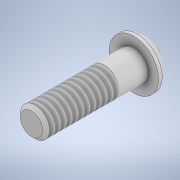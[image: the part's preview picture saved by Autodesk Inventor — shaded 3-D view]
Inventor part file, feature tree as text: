
AUTODESK INVENTOR PART (.ipt)
format: ipt  version: 2020 (Build 240168000, 168)  size: 140,288 bytes
history: native  units: in
note: dims shown in document units (in); Inventor stores cm internally (conversion verified against a paired STEP export)
features: sketch x2, revolve x1, extrude x1, chamfer x1, thread x1
ambient origin geometry x8: Origin, YZ Plane, XZ Plane, XY Plane, X Axis, Y Axis, Z Axis, Center Point
bodies: Solid1 (feature_tree)
feature tree (6):
  revolve  "Revolution1"  [1 undecoded]
  extrude  "Extrusion1"  Depth=0.125in
  chamfer  "Chamfer1"  Distance=0.125in
  thread  "Thread1"  [1 undecoded]
  sketch  "Sketch1"  dims[d0=1.0in d1=0.211in]
  sketch  "Sketch2"  dims[d2=0.031in d3=0.125in d4=0.125in d5=0.236in d6=0.125in d7=90.0deg d8=0.156in d9=0.111in d10=0.0in d11=0.03in d12=0.125in d13=45.0deg d14=1.0in d15=0.25in]
note: 2 required parameter values undecoded (feature->parameter linkage not recoverable at this tier; creation-order binding heuristic only, values carry confidence <= 0.55)